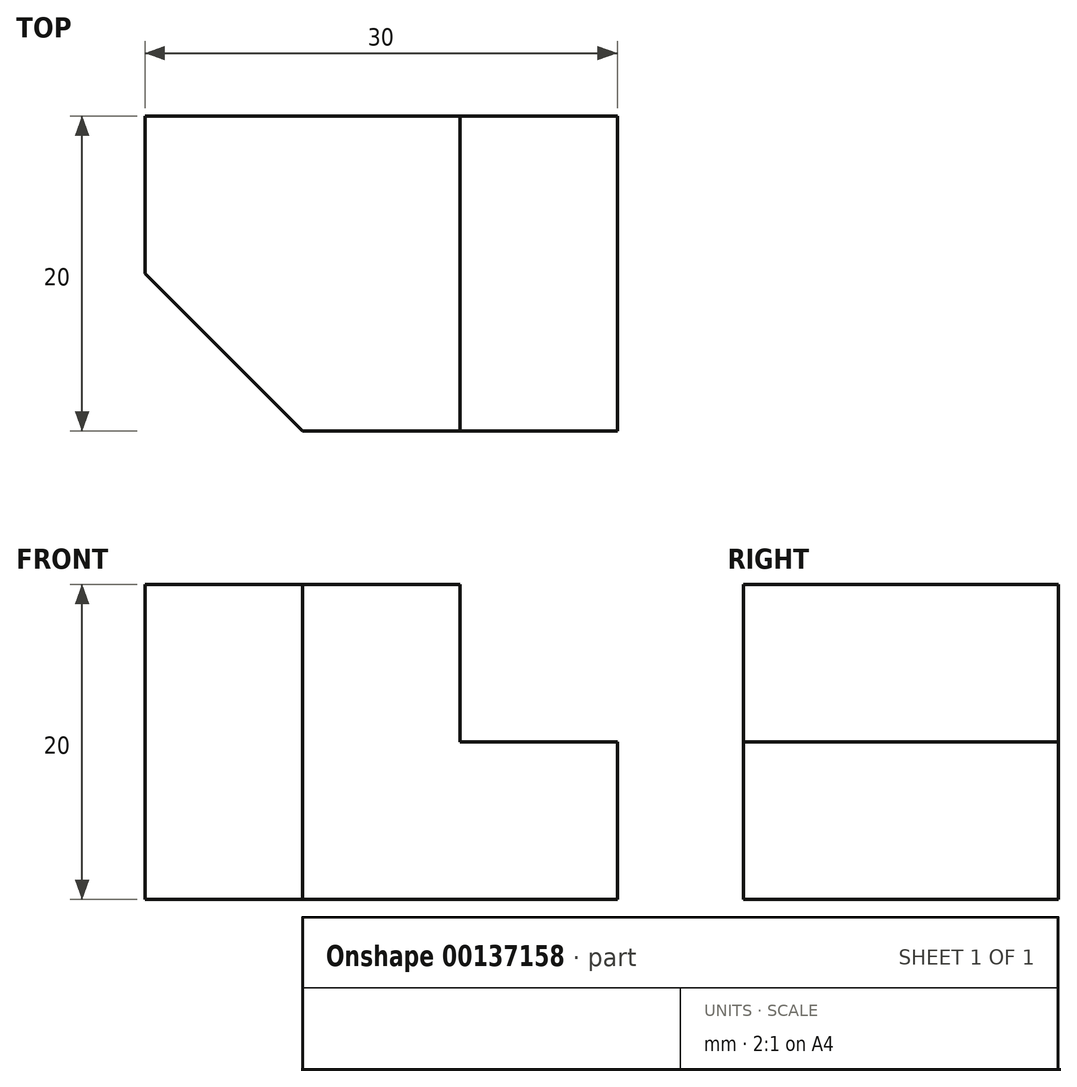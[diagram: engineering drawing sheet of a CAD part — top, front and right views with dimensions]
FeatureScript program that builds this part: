
annotation { "Feature Type Name" : "Feature", "Feature Type Description" : "" }
export const myFeature = defineFeature(function(context is Context, id is Id, definition is map)
    precondition{}
    {
        {
            var Q0;
            Q0=qCreatedBy(makeId("Top.planeOp"),FACE);
            var sketch = newSketch(context, id + "F0", { "sketchPlane" : qUnion([Q0])});
            skLineSegment(sketch, "E0", {"start": v(0, 0) * mm, "end": v(0, 10) * mm, "construction": true});
            skLineSegment(sketch, "E1", {"start": v(0, 0) * mm, "end": v(10, 0) * mm, "construction": true});
            skLineSegment(sketch, "E2", {"start": v(0, 10) * mm, "end": v(10, 0) * mm});
            skLineSegment(sketch, "E3", {"start": v(10, 0) * mm, "end": v(30, 0) * mm});
            skLineSegment(sketch, "E4", {"start": v(30, 0) * mm, "end": v(30, 20) * mm});
            skLineSegment(sketch, "E5", {"start": v(30, 20) * mm, "end": v(0, 20) * mm});
            skLineSegment(sketch, "E6", {"start": v(0, 20) * mm, "end": v(0, 10) * mm});
            skLineSegment(sketch, "E7", {"start": v(20, 0) * mm, "end": v(20, 20) * mm});
            skSolve(sketch);
        }
        {
            var Q0;
            {var subQ4=sQuery(id+"F0.wireOp",EDGE,"E2");Q0=makeQuery(id+"F0.imprint","IMPRINT",FACE,{"disambiguationData":[TD([[makeQuery(id+"F0.imprint","IMPRINT",EDGE,{"derivedFrom":subQ4}),1.0]])]});}
            extrude(context, id + "F1", {"entities" : qUnion([Q0]), "depth" : 20 * mm});
        }
        {
            var Q0;
            {var subQ0=sQuery(id+"F0.wireOp",EDGE,"E4");Q0=makeQuery(id+"F0.imprint","IMPRINT",FACE,{"disambiguationData":[TD([[makeQuery(id+"F0.imprint","IMPRINT",EDGE,{"derivedFrom":subQ0}),1.0]])]});}
            extrude(context, id + "F2", {"entities" : qUnion([Q0]), "operationType" : NewBodyOperationType.ADD, "depth" : 10 * mm});
        }
    });
